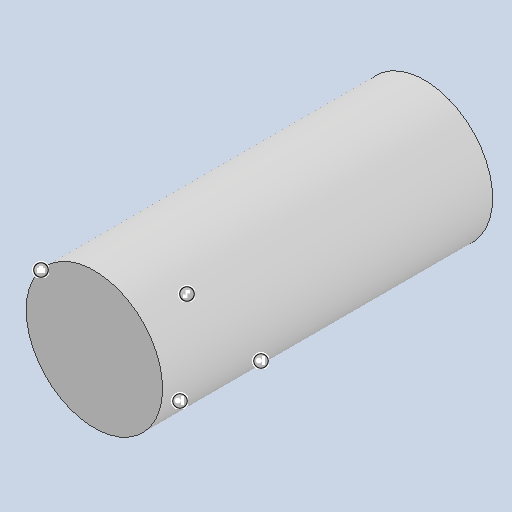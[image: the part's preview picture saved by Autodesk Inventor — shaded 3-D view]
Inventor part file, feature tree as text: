
AUTODESK INVENTOR PART (.ipt)
format: ipt  version: 2023 (Build 270158000, 158)  size: 100,352 bytes
history: native  units: mm
features: extrude x1, sketch x1
ambient origin geometry x8: Origin, YZ Plane, XZ Plane, XY Plane, X Axis, Y Axis, Z Axis, Center Point
bodies: Solid1 (feature_tree)
feature tree (2):
  extrude  "Extrusion1"  TaperAngle=0.0deg  [1 undecoded]
  sketch  "Sketch1"  dims[d2=0.0mm d3=0.0mm d4=0.0mm d9=0.0mm d10=0.0mm]
note: 1 required parameter value undecoded (feature->parameter linkage not recoverable at this tier; creation-order binding heuristic only, values carry confidence <= 0.55)
